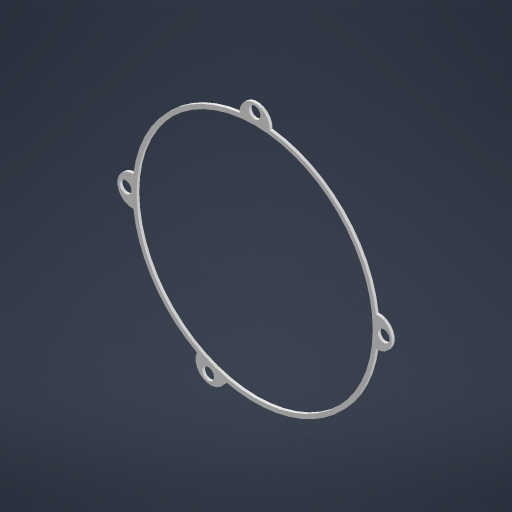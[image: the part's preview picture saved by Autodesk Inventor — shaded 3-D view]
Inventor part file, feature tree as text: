
AUTODESK INVENTOR PART (.ipt)
format: ipt  version: 2024.2 (Build 282272000, 272)  size: 244,224 bytes
history: native  units: in
note: dims shown in document units (in); Inventor stores cm internally (conversion verified against a paired STEP export)
features: other x4, extrude x2, sketch x2, reference x1
ambient origin geometry x8: Origin, YZ Plane, XZ Plane, XY Plane, X Axis, Y Axis, Z Axis, Center Point
bodies: Solid1 (feature_tree)
feature tree (9):
  extrude  "Extrusion1"  TaperAngle=0.0deg  [1 undecoded]
  extrude  "Extrusion2"  Depth=1.75in
  sketch  "Sketch1"  dims[d0=0.0591in d1=0.0in]
  reference  "Reference1"
  sketch  "Sketch2"  dims[d2=3.5in d3=1.75in d4=3.5in d5=0.0in d6=1.75in d7=0.4331in d8=0.4331in d10=0.4331in d11=0.0394in d12=0.0in d13=0.1693in d14=0.0985in d15=0.0in d16=0.1693in d18=0.1693in d19=0.0in d20=0.0985in d22=0.0985in d23=0.0in d24=0.0985in d25=0.0in d26=0.0in d27=0.4331in d28=0.4331in d29=1.75in d30=0.6299in d31=0.1693in d33=0.0985in d35=0.118in d36=0.2165in]
  other  "<userpath>\Desktop\Robotics\Swerve2\Assemblies\Pod.iam"
  other  "Pod.iam"
  other  "3ID3.5OD_Bearing:1"
  parser-record x1  (decoder bookkeeping rows leaked as tree rows — omitted from the tree; the rows remain in map.json)
note: 1 required parameter value undecoded (feature->parameter linkage not recoverable at this tier; creation-order binding heuristic only, values carry confidence <= 0.55)
